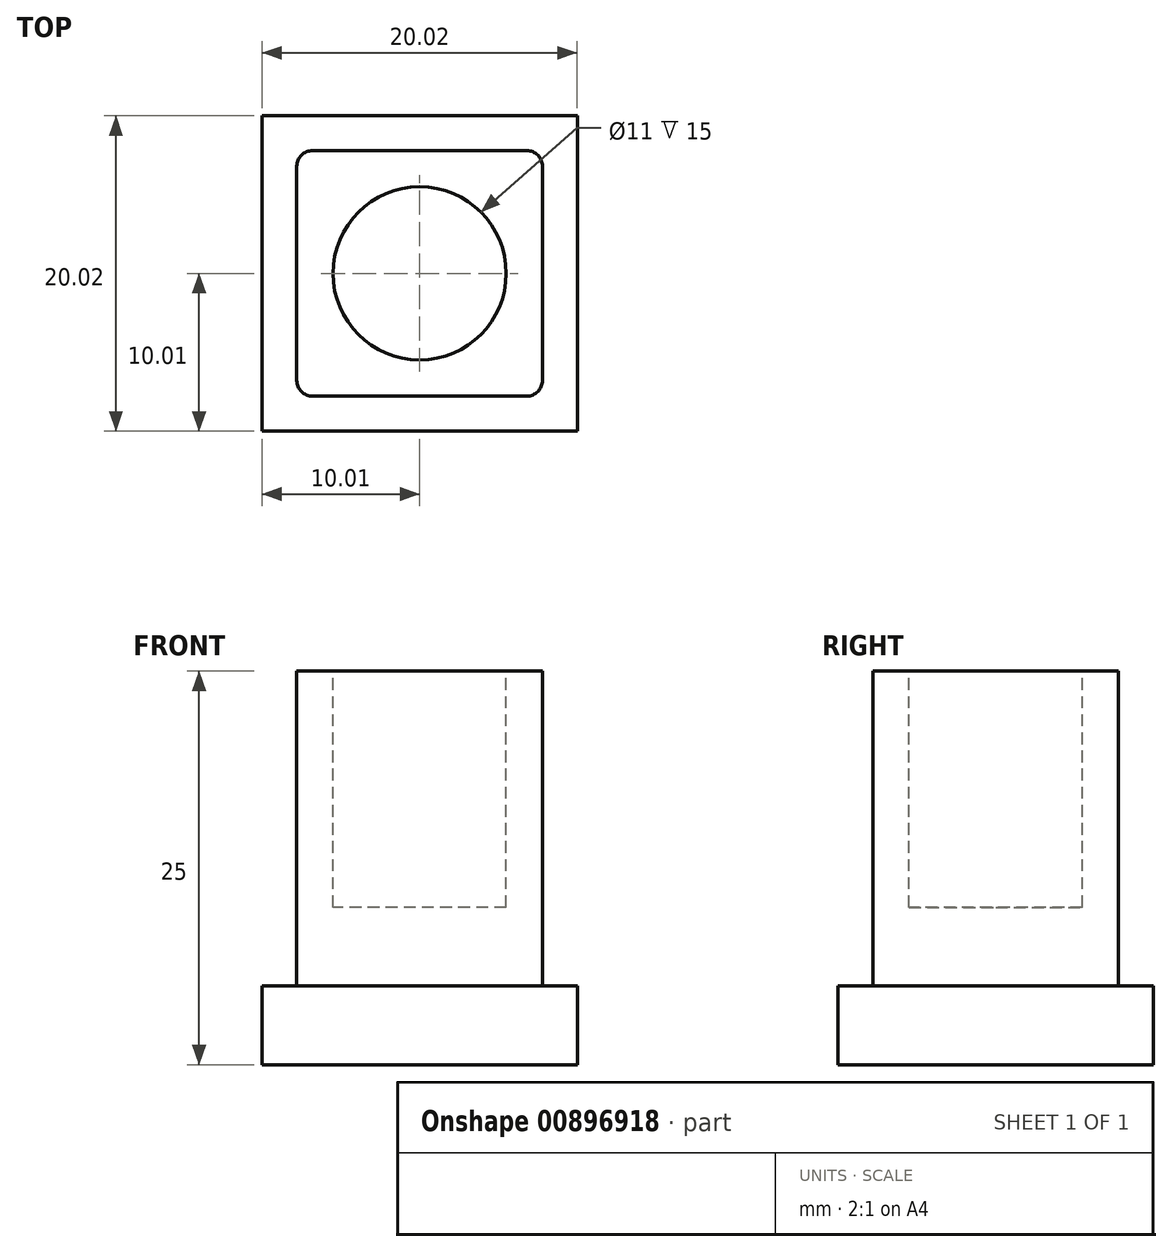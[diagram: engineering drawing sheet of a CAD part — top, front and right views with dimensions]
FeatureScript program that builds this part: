
annotation { "Feature Type Name" : "Feature", "Feature Type Description" : "" }
export const myFeature = defineFeature(function(context is Context, id is Id, definition is map)
    precondition{}
    {
        {
            var Q0;
            Q0=qCreatedBy(makeId("Top.planeOp"),FACE);
            var sketch = newSketch(context, id + "F0", { "sketchPlane" : qUnion([Q0])});
            skLineSegment(sketch, "E0.bottom", {"start": v(-10.02, 10.01) * mm, "end": v(10.02, 10.01) * mm});
            skLineSegment(sketch, "E0.top", {"start": v(-10.02, -10.02) * mm, "end": v(10.02, -10.02) * mm});
            skLineSegment(sketch, "E0.left", {"start": v(-10.02, 10.02) * mm, "end": v(-10.02, -10.02) * mm});
            skLineSegment(sketch, "E0.right", {"start": v(10.02, 10.02) * mm, "end": v(10.02, -10.02) * mm});
            skPoint(sketch, "E0.middle", {"position": v(0, 0) * mm});
            skSolve(sketch);
        }
        {
            var Q0;
            Q0=makeQuery(id+"F0.imprint","IMPRINT",FACE,{"disambiguationData":[TD([[makeQuery(id+"F0.imprint","IMPRINT",EDGE,{"derivedFrom":sQuery(id+"F0.wireOp",EDGE,"E0.bottom")}),-1.0]])]});
            extrude(context, id + "F1", {"entities" : qUnion([Q0]), "depth" : 5 * mm, "offsetDistance" : 25 * mm});
        }
        {
            var Q0;
            Q0=makeQuery(id+"F1.opExtrude","CAP_FACE",FACE,{"disambiguationData":[OSD([sQuery(id+"F0.wireOp",EDGE,"E0.bottom"),sQuery(id+"F0.wireOp",EDGE,"E0.top"),sQuery(id+"F0.wireOp",EDGE,"E0.left"),sQuery(id+"F0.wireOp",EDGE,"E0.right")])],"isStart":false});
            var sketch = newSketch(context, id + "F2", { "sketchPlane" : qUnion([Q0])});
            skLineSegment(sketch, "E1.bottom", {"start": v(-7.8, 7.8) * mm, "end": v(7.8, 7.8) * mm});
            skLineSegment(sketch, "E1.top", {"start": v(-7.8, -7.8) * mm, "end": v(7.8, -7.8) * mm});
            skLineSegment(sketch, "E1.left", {"start": v(-7.8, 7.8) * mm, "end": v(-7.8, -7.8) * mm});
            skLineSegment(sketch, "E1.right", {"start": v(7.8, 7.8) * mm, "end": v(7.8, -7.8) * mm});
            skPoint(sketch, "E1.middle", {"position": v(0, 0) * mm});
            skSolve(sketch);
        }
        {
            var Q0;
            Q0=makeQuery(id+"F2.imprint","IMPRINT",FACE,{"disambiguationData":[TD([[makeQuery(id+"F2.imprint","IMPRINT",EDGE,{"derivedFrom":sQuery(id+"F2.wireOp",EDGE,"E1.bottom")}),-1.0]])]});
            extrude(context, id + "F3", {"entities" : qUnion([Q0]), "operationType" : NewBodyOperationType.ADD, "depth" : 20 * mm, "offsetDistance" : 25 * mm});
        }
        {
            var Q0;
            Q0=makeQuery(id+"F3.opExtrude","CAP_FACE",FACE,{"disambiguationData":[OSD([sQuery(id+"F2.wireOp",EDGE,"E1.bottom"),sQuery(id+"F2.wireOp",EDGE,"E1.top"),sQuery(id+"F2.wireOp",EDGE,"E1.left"),sQuery(id+"F2.wireOp",EDGE,"E1.right")])],"isStart":false});
            var sketch = newSketch(context, id + "F4", { "sketchPlane" : qUnion([Q0])});
            skCircle(sketch, "E2", {"center": v(0, 0) * mm, "radius": 5.5 * mm});
            skSolve(sketch);
        }
        {
            var Q0;
            Q0=makeQuery(id+"F4.imprint","IMPRINT",FACE,{"disambiguationData":[TD([[makeQuery(id+"F4.imprint","IMPRINT",EDGE,{"derivedFrom":sQuery(id+"F4.wireOp",EDGE,"E2")}),1.0]])]});
            extrude(context, id + "F5", {"entities" : qUnion([Q0]), "operationType" : NewBodyOperationType.REMOVE, "oppositeDirection" : true, "depth" : 15 * mm, "offsetDistance" : 25 * mm});
        }
        {
            var Q0;
            Q0=makeQuery(id+"F3.opExtrude","SWEPT_EDGE",EDGE,{"disambiguationData":[OSD([sQuery(id+"F2.wireOp",EDGE,"E1.top"),sQuery(id+"F2.wireOp",EDGE,"E1.left")])]});
            var Q1;
            Q1=makeQuery(id+"F3.opExtrude","SWEPT_EDGE",EDGE,{"disambiguationData":[OSD([sQuery(id+"F2.wireOp",EDGE,"E1.top"),sQuery(id+"F2.wireOp",EDGE,"E1.right")])]});
            var Q2;
            Q2=makeQuery(id+"F3.opExtrude","SWEPT_EDGE",EDGE,{"disambiguationData":[OSD([sQuery(id+"F2.wireOp",EDGE,"E1.bottom"),sQuery(id+"F2.wireOp",EDGE,"E1.right")])]});
            var Q3;
            Q3=makeQuery(id+"F3.opExtrude","SWEPT_EDGE",EDGE,{"disambiguationData":[OSD([sQuery(id+"F2.wireOp",EDGE,"E1.bottom"),sQuery(id+"F2.wireOp",EDGE,"E1.left")])]});
            fillet(context, id + "F6", {"entities" : qUnion([Q0, Q1, Q2, Q3]), "radius" : 1 * mm, "tangentPropagation" : true, "allowEdgeOverflow" : false});
        }
    });
